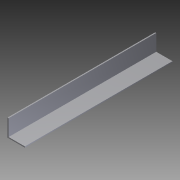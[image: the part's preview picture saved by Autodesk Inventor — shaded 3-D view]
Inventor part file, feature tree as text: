
AUTODESK INVENTOR PART (.ipt)
format: ipt  version: 2012 (Build 160160000, 160)  size: 73,216 bytes
history: native  units: in
note: dims shown in document units (in); Inventor stores cm internally (conversion verified against a paired STEP export)
features: extrude x1, sketch x1
ambient origin geometry x8: Origin, YZ Plane, XZ Plane, XY Plane, X Axis, Y Axis, Z Axis, Center Point
bodies: Solid1 (feature_tree)
feature tree (2):
  extrude  "Extrusion1"  Depth=0.9996in
  sketch  "Sketch1"  dims[d0=1.0in d1=0.9996in d2=0.0625in d3=0.0625in d4=8.5in d5=0.0in]
